FCSTD DOCUMENT  (FreeCAD 0.19R24276 (Git))
Label: PXX
License: All rights reserved
LicenseURL: http://en.wikipedia.org/wiki/All_rights_reserved
objects: Sketcher::SketchObject×1, PartDesign::Body×1
note: 2 computed .brp shape members not serialized (recipe doc carries the construction recipe); baked Part::Feature solids carry a one-line shape summary decoded from their .brp

FEATURE [Sketcher::SketchObject] Sketch
  FullyConstrained = true
  MapMode = 5
  Support = -> [XY_Plane]
  sketch-geometry (31):
    g0: LineSegment StartX=-150 StartY=16 StartZ=0 EndX=-150 EndY=-21 EndZ=0
    g1: LineSegment StartX=-148.5 StartY=-22.5 StartZ=0 EndX=148.5 EndY=-22.5 EndZ=0
    g2: LineSegment StartX=150 StartY=-21 StartZ=0 EndX=150 EndY=16 EndZ=0
    g3: LineSegment StartX=148.5 StartY=17.5 StartZ=0 EndX=30 EndY=17.5 EndZ=0
    g4: LineSegment StartX=30 StartY=17.5 StartZ=0 EndX=22.5 EndY=22.5 EndZ=0
    g5: LineSegment StartX=22.5 StartY=22.5 StartZ=0 EndX=-22.5 EndY=22.5 EndZ=0
    g6: LineSegment StartX=-22.5 StartY=22.5 StartZ=0 EndX=-30 EndY=17.5 EndZ=0
    g7: LineSegment StartX=-30 StartY=17.5 StartZ=0 EndX=-148.5 EndY=17.5 EndZ=0
    g8: ArcOfCircle CenterX=-148.5 CenterY=16 CenterZ=0 NormalX=0 NormalY=0 NormalZ=1 AngleXU=0 Radius=1.5 StartAngle=1.5708 EndAngle=3.14159
    g9: ArcOfCircle CenterX=-148.5 CenterY=-21 CenterZ=0 NormalX=0 NormalY=0 NormalZ=1 AngleXU=0 Radius=1.5 StartAngle=3.14159 EndAngle=4.71239
    g10: ArcOfCircle CenterX=148.5 CenterY=16 CenterZ=0 NormalX=0 NormalY=0 NormalZ=1 AngleXU=0 Radius=1.5 StartAngle=0 EndAngle=1.5708
    g11: ArcOfCircle CenterX=148.5 CenterY=-21 CenterZ=0 NormalX=0 NormalY=0 NormalZ=1 AngleXU=0 Radius=1.5 StartAngle=4.71239 EndAngle=6.28319
    g12: LineSegment StartX=-140 StartY=17.5 StartZ=0 EndX=-140 EndY=-22.5 EndZ=0
    g13: Circle CenterX=-140 CenterY=7.5 CenterZ=0 NormalX=0 NormalY=0 NormalZ=1 AngleXU=0 Radius=3
    g14: Circle CenterX=-140 CenterY=-12.5 CenterZ=0 NormalX=0 NormalY=0 NormalZ=1 AngleXU=0 Radius=3
    g15: LineSegment StartX=140 StartY=17.5 StartZ=0 EndX=140 EndY=-22.5 EndZ=0
    g16: Circle CenterX=140 CenterY=7.5 CenterZ=0 NormalX=0 NormalY=0 NormalZ=1 AngleXU=0 Radius=3
    g17: Circle CenterX=140 CenterY=-12.5 CenterZ=0 NormalX=0 NormalY=0 NormalZ=1 AngleXU=0 Radius=3
    g18: Circle CenterX=0 CenterY=0 CenterZ=0 NormalX=0 NormalY=0 NormalZ=1 AngleXU=0 Radius=11.5
    g19: LineSegment StartX=-15.5 StartY=15.5 StartZ=0 EndX=15.5 EndY=15.5 EndZ=0
    g20: LineSegment StartX=15.5 StartY=15.5 StartZ=0 EndX=15.5 EndY=-15.5 EndZ=0
    g21: LineSegment StartX=15.5 StartY=-15.5 StartZ=0 EndX=-15.5 EndY=-15.5 EndZ=0
    g22: LineSegment StartX=-15.5 StartY=-15.5 StartZ=0 EndX=-15.5 EndY=15.5 EndZ=0
    g23: Circle CenterX=-15.5 CenterY=15.5 CenterZ=0 NormalX=0 NormalY=0 NormalZ=1 AngleXU=0 Radius=1.75
    g24: Circle CenterX=15.5 CenterY=15.5 CenterZ=0 NormalX=0 NormalY=0 NormalZ=1 AngleXU=0 Radius=1.75
    g25: Circle CenterX=-15.5 CenterY=-15.5 CenterZ=0 NormalX=0 NormalY=0 NormalZ=1 AngleXU=0 Radius=1.75
    g26: Circle CenterX=15.5 CenterY=-15.5 CenterZ=0 NormalX=0 NormalY=0 NormalZ=1 AngleXU=0 Radius=1.75
    g27: LineSegment StartX=-22.5 StartY=22.5 StartZ=0 EndX=22.5 EndY=22.5 EndZ=0
    g28: LineSegment StartX=22.5 StartY=22.5 StartZ=0 EndX=22.5 EndY=-22.5 EndZ=0
    g29: LineSegment StartX=22.5 StartY=-22.5 StartZ=0 EndX=-22.5 EndY=-22.5 EndZ=0
    g30: LineSegment StartX=-22.5 StartY=-22.5 StartZ=0 EndX=-22.5 EndY=22.5 EndZ=0
  constraints (82):
    c: Vertical(g0)
    c: Horizontal(g1)
    c: Vertical(g2)
    c: Horizontal(g3)
    c: Coincident(g3,g4)
    c: Coincident(g4,g5)
    c: Horizontal(g5)
    c: Coincident(g5,g6)
    c: Coincident(g6,g7)
    c: Horizontal(g7)
    c: Tangent(g0,g8) = -1.5708
    c: Tangent(g7,g8) = -1.5708
    c: Tangent(g0,g9) = -1.5708
    c: Tangent(g1,g9) = -1.5708
    c: Tangent(g2,g10) = -1.5708
    c: Tangent(g3,g10) = -1.5708
    c: Tangent(g1,g11) = -1.5708
    c: Tangent(g2,g11) = -1.5708
    c: Equal(g8,g9)
    c: Equal(g9,g11)
    c: Equal(g11,g10)
    c: Diameter(g10) = 3
    c: Equal(g0,g2)
    c: Equal(g6,g4)
    c: DistanceY(g1,g7) = 40
    c: DistanceX(g0,g2) = 300
    c: DistanceX(g5,g5) = 45
    c: DistanceX(g6,g3) = 60
    c: DistanceX(g6,g-1) = 30
    c: DistanceY(g1,g5) = 45
    c: PointOnObject(g12,g7)
    c: PointOnObject(g12,g1)
    c: Vertical(g12)
    c: PointOnObject(g13,g12)
    c: PointOnObject(g14,g12)
    c: Diameter(g13) = 6
    c: Diameter(g14) = 6
    c: DistanceY(g14,g13) = 20
    c: DistanceY(g13,g7) = 10
    c: DistanceX(g0,g13) = 10
    c: PointOnObject(g15,g3)
    c: PointOnObject(g15,g1)
    c: Vertical(g15)
    c: PointOnObject(g16,g15)
    c: PointOnObject(g17,g15)
    c: Diameter(g16) = 6
    c: Diameter(g17) = 6
    c: DistanceY(g17,g16) = 20
    c: DistanceY(g16,g15) = 10
    c: DistanceX(g15,g2) = 10
    c: Equal(g7,g3)
    c: Coincident(g18,g-1)
    c: Diameter(g18) = 23
    c: Coincident(g19,g20)
    c: Coincident(g20,g21)
    c: Coincident(g21,g22)
    c: Coincident(g22,g19)
    c: Horizontal(g19)
    c: Horizontal(g21)
    c: Vertical(g20)
    c: Vertical(g22)
    c: DistanceX(g19,g19) = 31
    c: Equal(g19,g20)
    c: Symmetric(g19,g20,g18)
    c: Coincident(g23,g19)
    c: Coincident(g24,g19)
    c: Coincident(g25,g21)
    c: Coincident(g26,g20)
    c: Equal(g24,g23)
    c: Equal(g23,g25)
    c: Equal(g25,g26)
    c: Diameter(g24) = 3.5
    c: Coincident(g27,g28)
    c: Coincident(g28,g29)
    c: Coincident(g29,g30)
    c: Coincident(g30,g27)
    c: Horizontal(g29)
    c: Vertical(g30)
    c: Coincident(g27,g5)
    c: Coincident(g27,g4)
    c: Symmetric(g5,g28,g18)
    c: PointOnObject(g28,g1)
FEATURE [PartDesign::Body] Body
  Group = -> [Sketch]
  Origin = -> Origin
